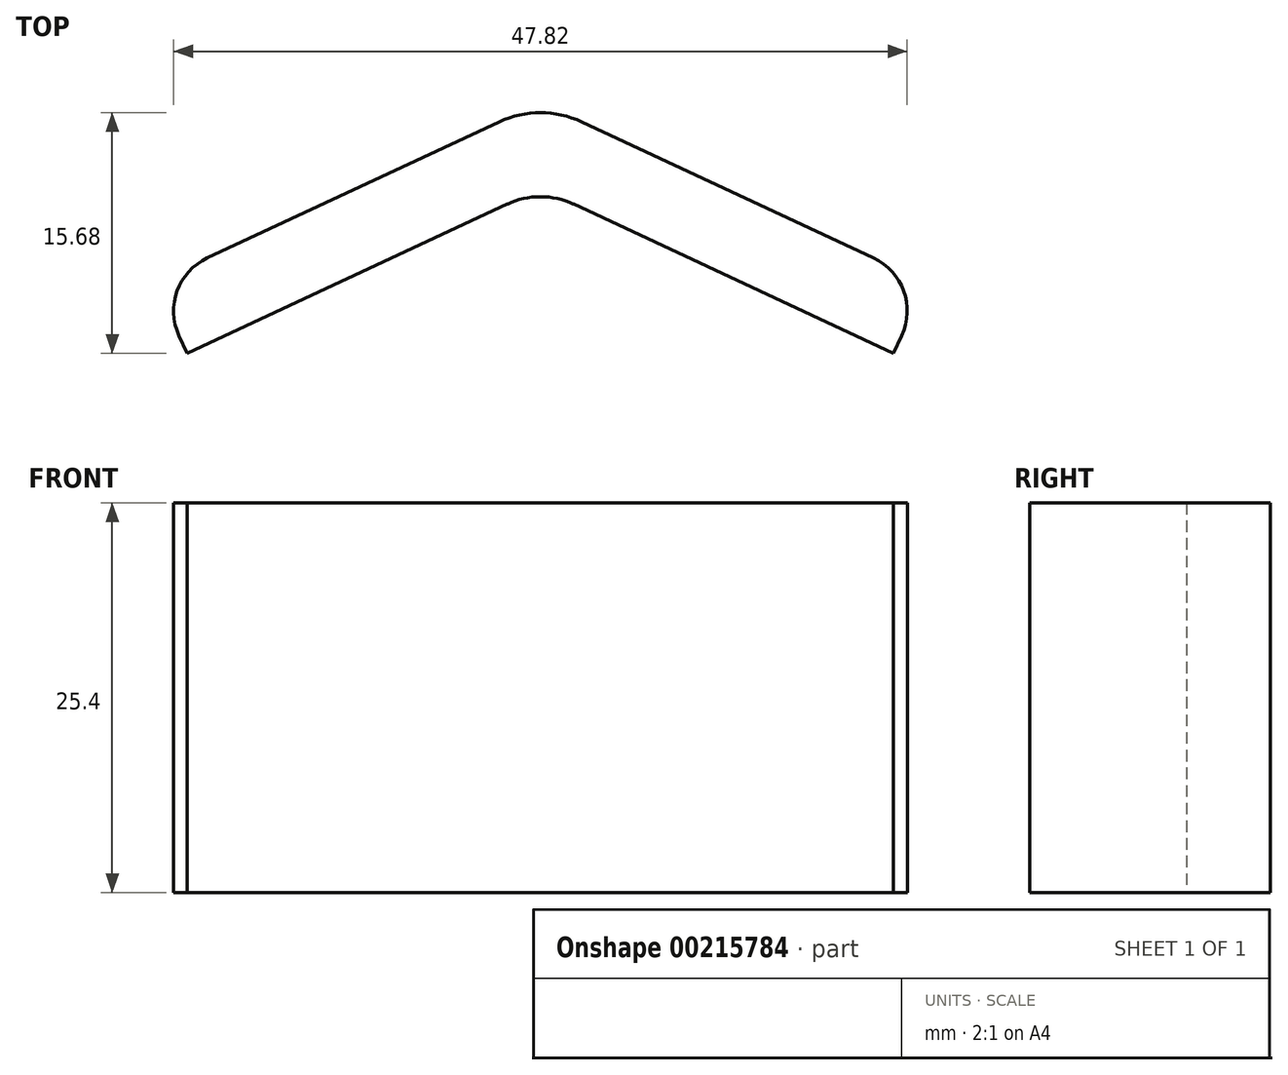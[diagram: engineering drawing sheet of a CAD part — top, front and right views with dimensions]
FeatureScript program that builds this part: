
annotation { "Feature Type Name" : "Feature", "Feature Type Description" : "" }
export const myFeature = defineFeature(function(context is Context, id is Id, definition is map)
    precondition{}
    {
        {
            var Q0;
            Q0=qCreatedBy(makeId("Top.planeOp"),FACE);
            var sketch = newSketch(context, id + "F0", { "sketchPlane" : qUnion([Q0])});
            skLineSegment(sketch, "E0", {"start": v(-2.15, -1) * mm, "end": v(-23.02, -10.73) * mm});
            skLineSegment(sketch, "E1", {"start": v(-23.02, -10.73) * mm, "end": v(-25.17, -6.13) * mm});
            skLineSegment(sketch, "E2", {"start": v(-25.17, -6.13) * mm, "end": v(-2.68, 4.35) * mm});
            skLineSegment(sketch, "E3.MirrorCS", {"start": v(25.17, -6.13) * mm, "end": v(2.68, 4.35) * mm});
            skLineSegment(sketch, "E4.MirrorCS", {"start": v(23.02, -10.73) * mm, "end": v(25.17, -6.13) * mm});
            skLineSegment(sketch, "E5.MirrorCS", {"start": v(2.15, -1) * mm, "end": v(23.02, -10.73) * mm});
            skPoint(sketch, "E6.visualSharp", {"position": v(0, 5.6) * mm});
            skArc(sketch, "E6.filletArc", {"start": v(2.68, 4.35) * mm, "mid": v(0, 4.95) * mm, "end": v(-2.68, 4.35) * mm});
            skPoint(sketch, "E7.visualSharp", {"position": v(0, 0) * mm});
            skArc(sketch, "E7.filletArc", {"start": v(2.15, -1) * mm, "mid": v(0, -0.53) * mm, "end": v(-2.15, -1) * mm});
            skSolve(sketch);
        }
        {
            var Q0;
            Q0=makeQuery(id+"F0.imprint","IMPRINT",FACE,{"disambiguationData":[TD([[makeQuery(id+"F0.imprint","IMPRINT",EDGE,{"derivedFrom":sQuery(id+"F0.wireOp",EDGE,"E0")}),-1.0]])]});
            extrude(context, id + "F1", {"entities" : qUnion([Q0]), "depth" : 25.4 * mm});
        }
        {
            var Q0;
            Q0=makeQuery(id+"F1.opExtrude","SWEPT_EDGE",EDGE,{"disambiguationData":[OSD([sQuery(id+"F0.wireOp",EDGE,"E1"),sQuery(id+"F0.wireOp",EDGE,"E2")])]});
            var Q1;
            Q1=makeQuery(id+"F1.opExtrude","SWEPT_EDGE",EDGE,{"disambiguationData":[OSD([sQuery(id+"F0.wireOp",EDGE,"E3.MirrorCS"),sQuery(id+"F0.wireOp",EDGE,"E4.MirrorCS")])]});
            fillet(context, id + "F2", {"entities" : qUnion([Q0, Q1]), "radius" : 3.8 * mm, "tangentPropagation" : true, "allowEdgeOverflow" : false});
        }
    });
